# Revit family: Magnus 2X Track Spot AC-DC - 3000K (Medium)
name_source: partatom
category: Lighting Fixtures
units: mm (PartAtom-declared; Revit-internal decimal feet)

## family parameters
Cut with Voids When Loaded = No
Host = Face
Light Source = No
Part Type = Normal
Room Calculation Point = No
Round Connector Dimension = Use Diameter
Shared = No

## types (1)
- Magnus 2X Track Spot AC-DC - 3000K (Medium)
    Beam Angle Degree = 49.6
    Bining = ≤3SDCM
    CCT(K) = 3000
    CRI = 90
    Certification = Available on request
    Colors = Metalic Chrome, Black, White
    Default Elevation = 1219 mm
    Driver Type = On-Off/ Dali 2.0/DT8.0/BLE
    Driving Current( mA) = 350
    Efficacy (Lm/W) = 83.68
    Efficiency = >92 %
    IP Rating = IP20
    Lamp Flux( lm) = 813.789
    Lifetime = L80/B10(>50,000hrs@Ta-30Deg C)
    Manufacturer = pluslighttech.
    THD = <10%
    Tilt Angle = 10.00°
    Tuneable & Dimmable = Yes
    UGR = <22
    URL = https://pluslighttech.com
    Wattage(W) = 10

## geometry (parser evidence)
native form markers: Sweep x112
no freeform markers — native parametric forms only
